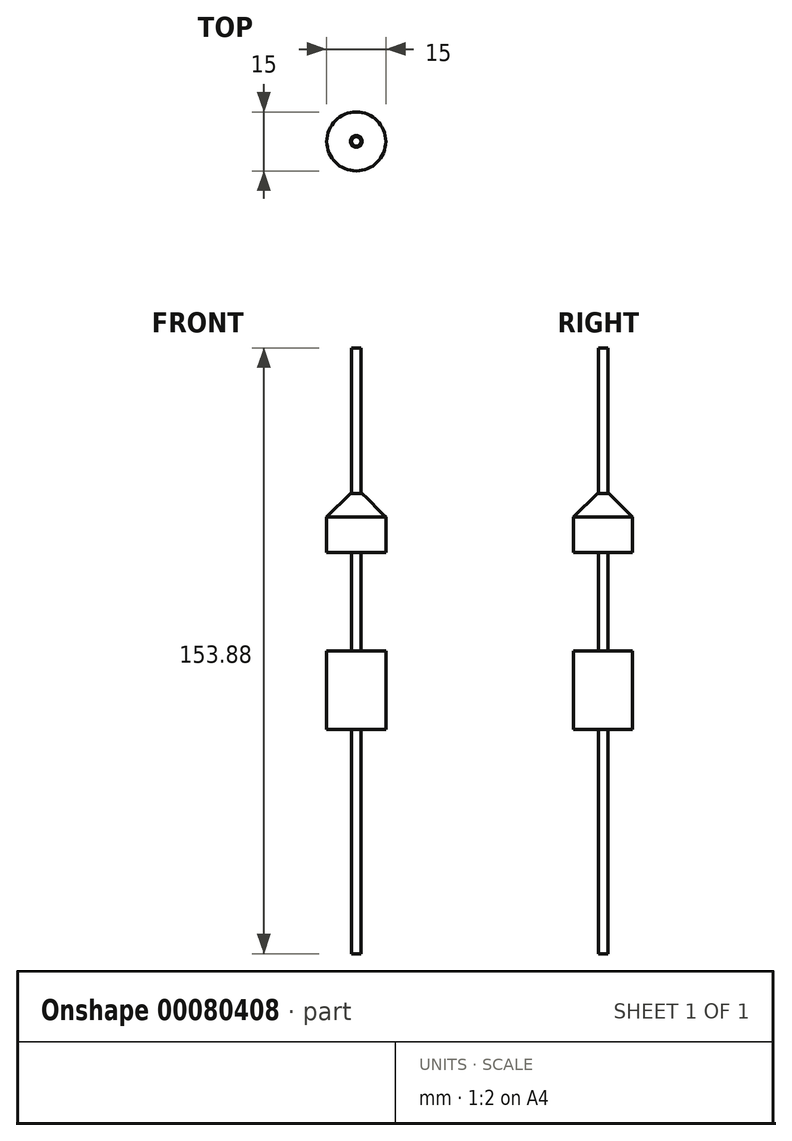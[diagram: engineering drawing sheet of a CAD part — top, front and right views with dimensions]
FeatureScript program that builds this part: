
annotation { "Feature Type Name" : "Feature", "Feature Type Description" : "" }
export const myFeature = defineFeature(function(context is Context, id is Id, definition is map)
    precondition{}
    {
        {
            var Q0;
            Q0=qCreatedBy(makeId("Top.planeOp"),FACE);
            var sketch = newSketch(context, id + "F0", { "sketchPlane" : qUnion([Q0])});
            skCircle(sketch, "E0", {"center": v(0, 0) * mm, "radius": 7.5 * mm});
            skSolve(sketch);
        }
        {
            var Q0;
            Q0 = qSketchRegion(id + "F0", true);
            extrude(context, id + "F1", {"entities" : qUnion([Q0]), "oppositeDirection" : true, "depth" : 20 * mm});
        }
        {
            var Q0;
            Q0=qCreatedBy(makeId("Top.planeOp"),FACE);
            var sketch = newSketch(context, id + "F2", { "sketchPlane" : qUnion([Q0])});
            skCircle(sketch, "E1", {"center": v(0, 0) * mm, "radius": 1.2 * mm});
            skSolve(sketch);
        }
        {
            var Q0;
            Q0 = qSketchRegion(id + "F2", true);
            extrude(context, id + "F3", {"entities" : qUnion([Q0]), "operationType" : NewBodyOperationType.ADD, "endBound" : BoundingType.SYMMETRIC, "depth" : 153.89 * mm});
        }
        {
            var Q0;
            Q0=qCreatedBy(makeId("Top.planeOp"),FACE);
            cPlane(context, id + "F4", {"entities" : qUnion([Q0]), "cplaneType" : CPlaneType.OFFSET, "offset" : 25 * mm, "width" : 150 * mm, "height" : 150 * mm});
        }
        {
            var Q0;
            Q0=qCreatedBy(id+"F4.planeOp",FACE);
            var sketch = newSketch(context, id + "F5", { "sketchPlane" : qUnion([Q0])});
            skCircle(sketch, "E2", {"center": v(0, 0) * mm, "radius": 7.5 * mm});
            skSolve(sketch);
        }
        {
            var Q0;
            Q0 = qSketchRegion(id + "F5", true);
            extrude(context, id + "F6", {"entities" : qUnion([Q0]), "operationType" : NewBodyOperationType.ADD, "depth" : 15 * mm});
        }
        {
            var Q0;
            Q0=makeQuery(id+"F6.opExtrude","CAP_EDGE",EDGE,{"disambiguationData":[OSD([sQuery(id+"F5.wireOp",EDGE,"E2")])],"isStart":false});
            chamfer(context, id + "F7", {"entities" : qUnion([Q0]), "width" : 6 * mm, "tangentPropagation" : true});
        }
    });
